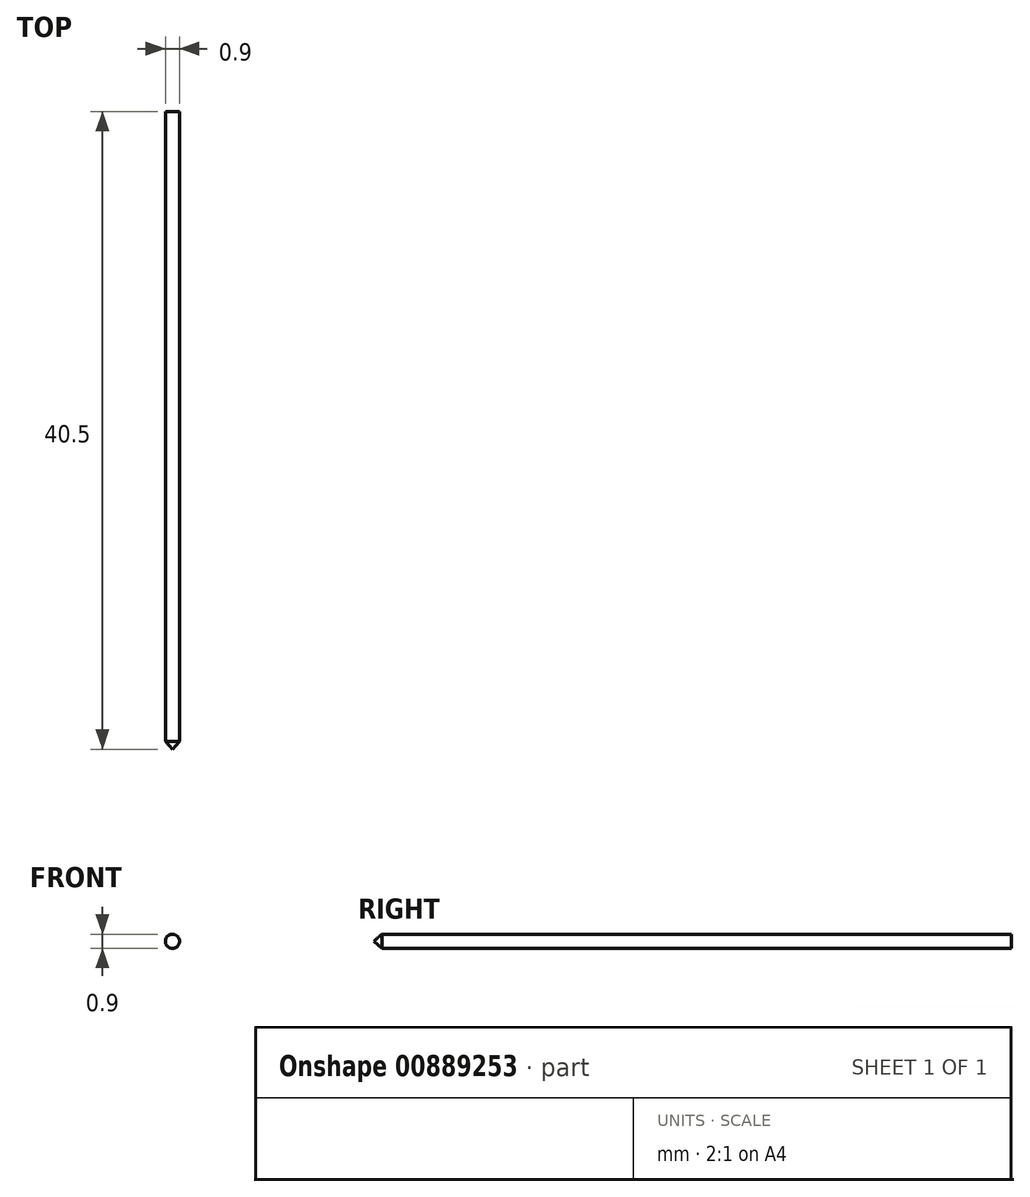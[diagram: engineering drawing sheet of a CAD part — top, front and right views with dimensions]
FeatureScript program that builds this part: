
annotation { "Feature Type Name" : "Feature", "Feature Type Description" : "" }
export const myFeature = defineFeature(function(context is Context, id is Id, definition is map)
    precondition{}
    {
        {
            var Q0;
            Q0=qCreatedBy(makeId("Front.planeOp"),FACE);
            var sketch = newSketch(context, id + "F0", { "sketchPlane" : qUnion([Q0])});
            skCircle(sketch, "E0", {"center": v(0, 0) * mm, "radius": 0.45 * mm});
            skSolve(sketch);
        }
        {
            var Q0;
            Q0=makeQuery(id+"F0.imprint","IMPRINT",FACE,{"disambiguationData":[TD([[makeQuery(id+"F0.imprint","IMPRINT",EDGE,{"derivedFrom":sQuery(id+"F0.wireOp",EDGE,"E0")}),1.0]])]});
            extrude(context, id + "F1", {"entities" : qUnion([Q0]), "depth" : 40 * mm, "offsetDistance" : 25 * mm});
        }
        {
            var Q0;
            Q0=qCreatedBy(makeId("Right.planeOp"),FACE);
            var sketch = newSketch(context, id + "F2", { "sketchPlane" : qUnion([Q0])});
            skLineSegment(sketch, "E1", {"start": v(-40, 0) * mm, "end": v(-40.5, 0) * mm});
            skLineSegment(sketch, "E2", {"start": v(-40.5, 0) * mm, "end": v(-40, 0.45) * mm});
            skLineSegment(sketch, "E3", {"start": v(-40, 0.45) * mm, "end": v(-40, 0) * mm});
            skSolve(sketch);
        }
        {
            var Q0;
            Q0=makeQuery(id+"F2.imprint","IMPRINT",FACE,{"disambiguationData":[TD([[makeQuery(id+"F2.imprint","IMPRINT",EDGE,{"derivedFrom":sQuery(id+"F2.wireOp",EDGE,"E1")}),-1.0]])]});
            var Q1;
            Q1=sQuery(id+"F2.wireOp",EDGE,"E1");
            revolve(context, id + "F3", {"operationType" : NewBodyOperationType.ADD, "surfaceOperationType" : NewSurfaceOperationType.NEW, "entities" : qUnion([Q0]), "axis" : qUnion([Q1]), "revolveType" : RevolveType.FULL});
        }
    });
